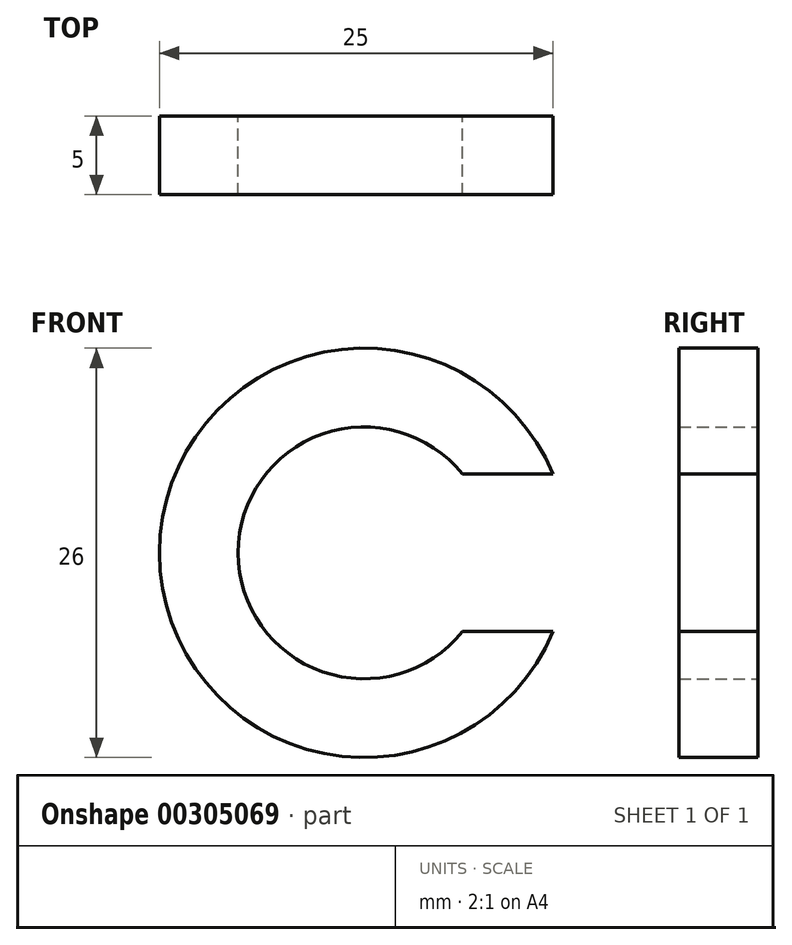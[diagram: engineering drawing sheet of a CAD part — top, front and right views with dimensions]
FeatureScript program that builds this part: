
annotation { "Feature Type Name" : "Feature", "Feature Type Description" : "" }
export const myFeature = defineFeature(function(context is Context, id is Id, definition is map)
    precondition{}
    {
        {
            var Q0;
            Q0=qCreatedBy(makeId("Front.planeOp"),FACE);
            var sketch = newSketch(context, id + "F0", { "sketchPlane" : qUnion([Q0])});
            skCircle(sketch, "E0", {"center": v(0, 0) * mm, "radius": 13 * mm});
            skCircle(sketch, "E1.0", {"center": v(0, 0) * mm, "radius": 8 * mm});
            skLineSegment(sketch, "E2", {"start": v(8, 0) * mm, "end": v(13, 0) * mm, "construction": true});
            skLineSegment(sketch, "E3", {"start": v(6.24, 5) * mm, "end": v(12, 5) * mm});
            skLineSegment(sketch, "E4", {"start": v(12, -5) * mm, "end": v(6.24, -5) * mm});
            skSolve(sketch);
        }
        {
            var Q0;
            {var subQ0=sQuery(id+"F0.wireOp",EDGE,"E3");Q0=makeQuery(id+"F0.imprint","IMPRINT",FACE,{"disambiguationData":[TD([[makeQuery(id+"F0.imprint","IMPRINT",EDGE,{"derivedFrom":subQ0}),1.0]])]});}
            extrude(context, id + "F1", {"entities" : qUnion([Q0]), "depth" : 5 * mm});
        }
    });
